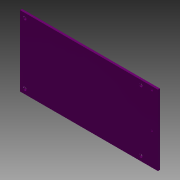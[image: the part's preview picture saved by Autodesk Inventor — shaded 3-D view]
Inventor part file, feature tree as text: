
AUTODESK INVENTOR PART (.ipt)
format: ipt  version: 2015 (Build 190159000, 159)  size: 135,680 bytes
history: native  units: in
note: dims shown in document units (in); Inventor stores cm internally (conversion verified against a paired STEP export)
features: extrude x2, sketch x2
ambient origin geometry x8: Origin, YZ Plane, XZ Plane, XY Plane, X Axis, Y Axis, Z Axis, Center Point
bodies: Solid1 (feature_tree)
feature tree (4):
  extrude  "Extrusion1"  Depth=4.4in
  extrude  "Extrusion3"  Depth=2.25in
  sketch  "Sketch1"  dims[d0=0.0646in d1=0.0in d2=4.4in]
  sketch  "Sketch3"  dims[d4=2.25in d5=1.95in d6=0.1102in d8=0.1102in d10=1.95in d15=0.0787in d16=0.1969in d17=0.1969in d18=0.0394in d19=0.1181in d20=0.0in d21=0.15in d22=0.15in d23=0.15in d28=0.15in d30=2.5in d33=1.3469in d34=1.3469in d35=0.078in d36=0.2in d37=0.1067in d38=0.1102in d39=0.15in d40=0.55in d41=2.5in d42=0.063in d43=0.2in d44=0.1067in]
